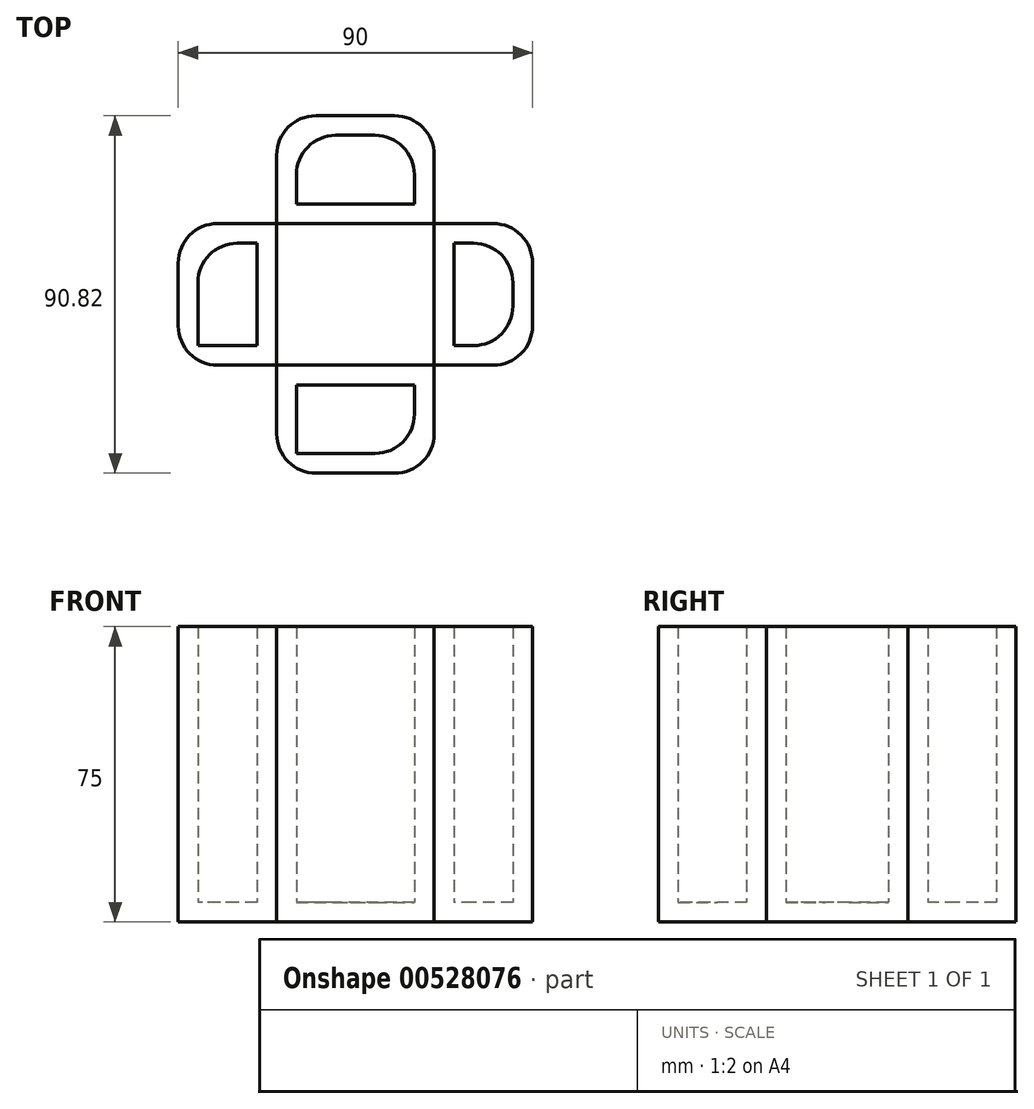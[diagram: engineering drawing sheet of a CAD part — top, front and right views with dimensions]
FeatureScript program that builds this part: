
annotation { "Feature Type Name" : "Feature", "Feature Type Description" : "" }
export const myFeature = defineFeature(function(context is Context, id is Id, definition is map)
    precondition{}
    {
        {
            var Q0;
            Q0=qCreatedBy(makeId("Top.planeOp"),FACE);
            var sketch = newSketch(context, id + "F0", { "sketchPlane" : qUnion([Q0])});
            skLineSegment(sketch, "E0.bottom", {"start": v(45, 18) * mm, "end": v(-45, 18) * mm});
            skLineSegment(sketch, "E0.top", {"start": v(45, -18) * mm, "end": v(-45, -18) * mm});
            skLineSegment(sketch, "E0.left", {"start": v(45, 18) * mm, "end": v(45, -18) * mm});
            skLineSegment(sketch, "E0.right", {"start": v(-45, 18) * mm, "end": v(-45, -18) * mm});
            skPoint(sketch, "E0.middle", {"position": v(0, 0) * mm});
            skLineSegment(sketch, "E1.bottom", {"start": v(-20, 45.41) * mm, "end": v(20, 45.41) * mm});
            skLineSegment(sketch, "E1.top", {"start": v(-20, -45.41) * mm, "end": v(20, -45.41) * mm});
            skLineSegment(sketch, "E1.left", {"start": v(-20, 45.41) * mm, "end": v(-20, -45.41) * mm});
            skLineSegment(sketch, "E1.right", {"start": v(20, 45.41) * mm, "end": v(20, -45.41) * mm});
            skSolve(sketch);
        }
        {
            var Q0;
            {var subQ5=sQuery(id+"F0.wireOp",EDGE,"E1.bottom");Q0=makeQuery(id+"F0.imprint","IMPRINT",FACE,{"disambiguationData":[TD([[makeQuery(id+"F0.imprint","IMPRINT",EDGE,{"derivedFrom":subQ5}),-1.0]])]});}
            var Q1;
            {var subQ0=sQuery(id+"F0.wireOp",EDGE,"E0.left");Q1=makeQuery(id+"F0.imprint","IMPRINT",FACE,{"disambiguationData":[TD([[makeQuery(id+"F0.imprint","IMPRINT",EDGE,{"derivedFrom":subQ0}),-1.0]])]});}
            var Q2;
            {var subQ0=sQuery(id+"F0.wireOp",EDGE,"E0.right");Q2=makeQuery(id+"F0.imprint","IMPRINT",FACE,{"disambiguationData":[TD([[makeQuery(id+"F0.imprint","IMPRINT",EDGE,{"derivedFrom":subQ0}),1.0]])]});}
            var Q3;
            {var subQ5=sQuery(id+"F0.wireOp",EDGE,"E1.top");Q3=makeQuery(id+"F0.imprint","IMPRINT",FACE,{"disambiguationData":[TD([[makeQuery(id+"F0.imprint","IMPRINT",EDGE,{"derivedFrom":subQ5}),1.0]])]});}
            extrude(context, id + "F1", {"entities" : qUnion([Q0, Q1, Q2, Q3]), "depth" : 75 * mm, "offsetDistance" : 25 * mm});
        }
        {
            var Q0;
            Q0=makeQuery(id+"F1.opExtrude","CAP_FACE",FACE,{"disambiguationData":[OSD([sQuery(id+"F0.wireOp",EDGE,"E0.top"),sQuery(id+"F0.wireOp",EDGE,"E1.top"),sQuery(id+"F0.wireOp",EDGE,"E1.left"),sQuery(id+"F0.wireOp",EDGE,"E1.right")])],"isStart":false});
            var Q1;
            Q1=makeQuery(id+"F1.opExtrude","CAP_FACE",FACE,{"disambiguationData":[OSD([sQuery(id+"F0.wireOp",EDGE,"E0.bottom"),sQuery(id+"F0.wireOp",EDGE,"E0.top"),sQuery(id+"F0.wireOp",EDGE,"E0.left"),sQuery(id+"F0.wireOp",EDGE,"E1.right")])],"isStart":false});
            var Q2;
            Q2=makeQuery(id+"F1.opExtrude","CAP_FACE",FACE,{"disambiguationData":[OSD([sQuery(id+"F0.wireOp",EDGE,"E0.bottom"),sQuery(id+"F0.wireOp",EDGE,"E1.bottom"),sQuery(id+"F0.wireOp",EDGE,"E1.left"),sQuery(id+"F0.wireOp",EDGE,"E1.right")])],"isStart":false});
            var Q3;
            Q3=makeQuery(id+"F1.opExtrude","CAP_FACE",FACE,{"disambiguationData":[OSD([sQuery(id+"F0.wireOp",EDGE,"E0.bottom"),sQuery(id+"F0.wireOp",EDGE,"E0.top"),sQuery(id+"F0.wireOp",EDGE,"E0.right"),sQuery(id+"F0.wireOp",EDGE,"E1.left")])],"isStart":false});
            shell(context, id + "F2", {"entities" : qUnion([Q0, Q1, Q2, Q3]), "thickness" : 5 * mm});
        }
        {
            var Q0;
            Q0=makeQuery(id+"F1.opExtrude","SWEPT_EDGE",EDGE,{"disambiguationData":[OSD([sQuery(id+"F0.wireOp",EDGE,"E0.bottom"),sQuery(id+"F0.wireOp",EDGE,"E0.left")])]});
            var Q1;
            Q1=makeQuery(id+"F1.opExtrude","SWEPT_EDGE",EDGE,{"disambiguationData":[OSD([sQuery(id+"F0.wireOp",EDGE,"E0.top"),sQuery(id+"F0.wireOp",EDGE,"E0.left")])]});
            var Q2;
            Q2=makeQuery(id+"F1.opExtrude","SWEPT_EDGE",EDGE,{"disambiguationData":[OSD([sQuery(id+"F0.wireOp",EDGE,"E1.bottom"),sQuery(id+"F0.wireOp",EDGE,"E1.right")])]});
            var Q3;
            Q3=makeQuery(id+"F1.opExtrude","SWEPT_EDGE",EDGE,{"disambiguationData":[OSD([sQuery(id+"F0.wireOp",EDGE,"E1.bottom"),sQuery(id+"F0.wireOp",EDGE,"E1.left")])]});
            var Q4;
            Q4=makeQuery(id+"F1.opExtrude","SWEPT_EDGE",EDGE,{"disambiguationData":[OSD([sQuery(id+"F0.wireOp",EDGE,"E0.bottom"),sQuery(id+"F0.wireOp",EDGE,"E0.right")])]});
            var Q5;
            Q5=makeQuery(id+"F1.opExtrude","SWEPT_EDGE",EDGE,{"disambiguationData":[OSD([sQuery(id+"F0.wireOp",EDGE,"E1.top"),sQuery(id+"F0.wireOp",EDGE,"E1.right")])]});
            var Q6;
            Q6=makeQuery(id+"F1.opExtrude","SWEPT_EDGE",EDGE,{"disambiguationData":[OSD([sQuery(id+"F0.wireOp",EDGE,"E1.top"),sQuery(id+"F0.wireOp",EDGE,"E1.left")])]});
            var Q7;
            Q7=makeQuery(id+"F1.opExtrude","SWEPT_EDGE",EDGE,{"disambiguationData":[OSD([sQuery(id+"F0.wireOp",EDGE,"E0.top"),sQuery(id+"F0.wireOp",EDGE,"E0.right")])]});
            var Q8;
            Q8=makeQuery(id+"F2.opShell","OFFSET_EDGE",EDGE,{"disambiguationData":[OSD([sQuery(id+"F0.wireOp",EDGE,"E0.top"),sQuery(id+"F0.wireOp",EDGE,"E0.left")])]});
            var Q9;
            Q9=makeQuery(id+"F2.opShell","OFFSET_EDGE",EDGE,{"disambiguationData":[OSD([sQuery(id+"F0.wireOp",EDGE,"E1.top"),sQuery(id+"F0.wireOp",EDGE,"E1.right")])]});
            var Q10;
            Q10=makeQuery(id+"F2.opShell","OFFSET_EDGE",EDGE,{"disambiguationData":[OSD([sQuery(id+"F0.wireOp",EDGE,"E1.bottom"),sQuery(id+"F0.wireOp",EDGE,"E1.right")])]});
            var Q11;
            Q11=makeQuery(id+"F2.opShell","OFFSET_EDGE",EDGE,{"disambiguationData":[OSD([sQuery(id+"F0.wireOp",EDGE,"E0.bottom"),sQuery(id+"F0.wireOp",EDGE,"E0.left")])]});
            var Q12;
            Q12=makeQuery(id+"F2.opShell","OFFSET_EDGE",EDGE,{"disambiguationData":[OSD([sQuery(id+"F0.wireOp",EDGE,"E0.bottom"),sQuery(id+"F0.wireOp",EDGE,"E0.right")])]});
            var Q13;
            Q13=makeQuery(id+"F2.opShell","OFFSET_EDGE",EDGE,{"disambiguationData":[OSD([sQuery(id+"F0.wireOp",EDGE,"E1.bottom"),sQuery(id+"F0.wireOp",EDGE,"E1.left")])]});
            fillet(context, id + "F3", {"entities" : qUnion([Q0, Q1, Q2, Q3, Q4, Q5, Q6, Q7, Q8, Q9, Q10, Q11, Q12, Q13]), "radius" : 10 * mm, "tangentPropagation" : true, "allowEdgeOverflow" : false});
        }
    });
